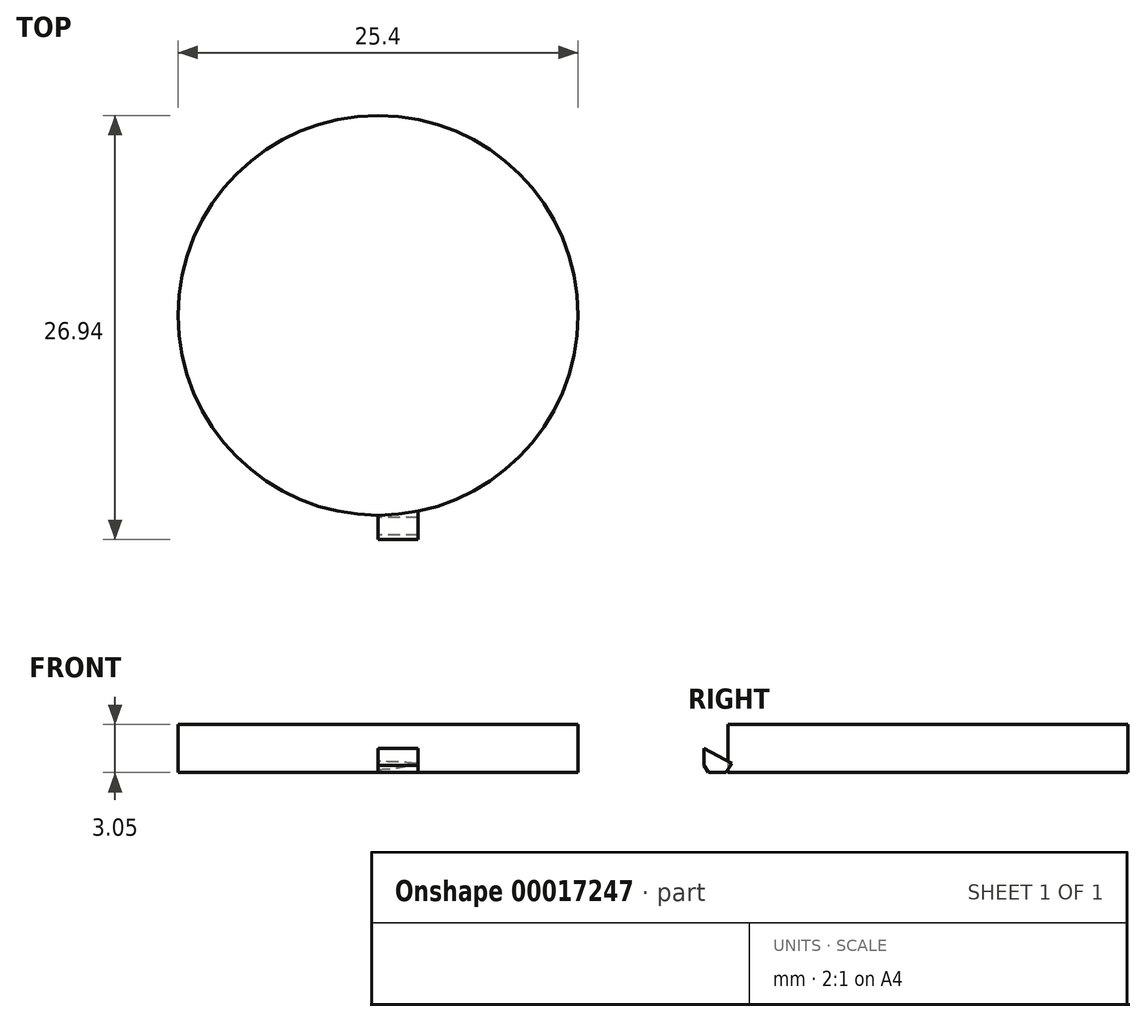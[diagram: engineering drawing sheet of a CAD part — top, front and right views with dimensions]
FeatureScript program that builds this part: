
annotation { "Feature Type Name" : "Feature", "Feature Type Description" : "" }
export const myFeature = defineFeature(function(context is Context, id is Id, definition is map)
    precondition{}
    {
        {
            var Q0;
            Q0=qCreatedBy(makeId("Top.planeOp"),FACE);
            var sketch = newSketch(context, id + "F0", { "sketchPlane" : qUnion([Q0])});
            skCircle(sketch, "E0", {"center": v(0, 0) * mm, "radius": 12.7 * mm});
            skSolve(sketch);
        }
        {
            var Q0;
            Q0 = qSketchRegion(id + "F0", true);
            extrude(context, id + "F1", {"entities" : qUnion([Q0]), "depth" : 3.05 * mm});
        }
        {
            var Q0;
            Q0=qCreatedBy(makeId("Right.planeOp"),FACE);
            var sketch = newSketch(context, id + "F2", { "sketchPlane" : qUnion([Q0])});
            skLineSegment(sketch, "E1", {"start": v(-14.24, 0.46) * mm, "end": v(-13.94, 0) * mm});
            skLineSegment(sketch, "E2", {"start": v(-14.24, 1.52) * mm, "end": v(-14.24, 0.46) * mm});
            skLineSegment(sketch, "E3", {"start": v(-12.84, 0) * mm, "end": v(-12.46, 0.57) * mm});
            skLineSegment(sketch, "E4", {"start": v(-12.46, 0.57) * mm, "end": v(-14.24, 1.52) * mm});
            skLineSegment(sketch, "E5", {"start": v(-13.94, 0) * mm, "end": v(-12.84, 0) * mm});
            skSolve(sketch);
        }
        {
            var Q0;
            Q0 = qSketchRegion(id + "F2", true);
            extrude(context, id + "F3", {"entities" : qUnion([Q0]), "operationType" : NewBodyOperationType.ADD, "depth" : 2.54 * mm});
        }
    });
